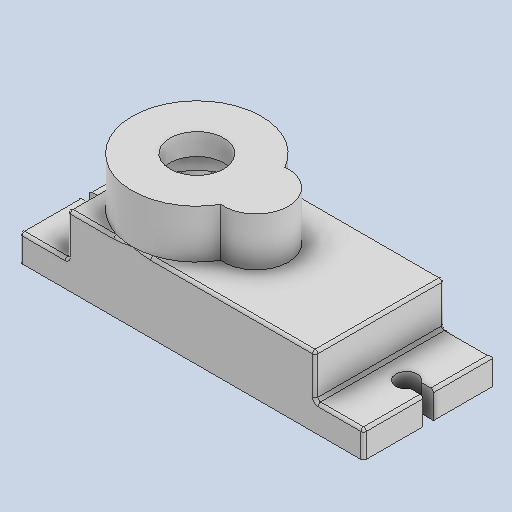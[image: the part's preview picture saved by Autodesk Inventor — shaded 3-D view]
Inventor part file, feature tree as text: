
AUTODESK INVENTOR PART (.ipt)
format: ipt  version: 2025.2 (Build 292293000, 293)  size: 869,376 bytes
history: native  units: mm
features: other x1, thread x1
ambient origin geometry x8: Origin, YZ Plane, XZ Plane, XY Plane, X Axis, Y Axis, Z Axis, Center Point
bodies: Body1 (feature_tree)
feature tree (2):
  other  "Bryła1"
  thread  "Thread4"  [1 undecoded]
note: 1 required parameter value undecoded (feature->parameter linkage not recoverable at this tier; creation-order binding heuristic only, values carry confidence <= 0.55)
